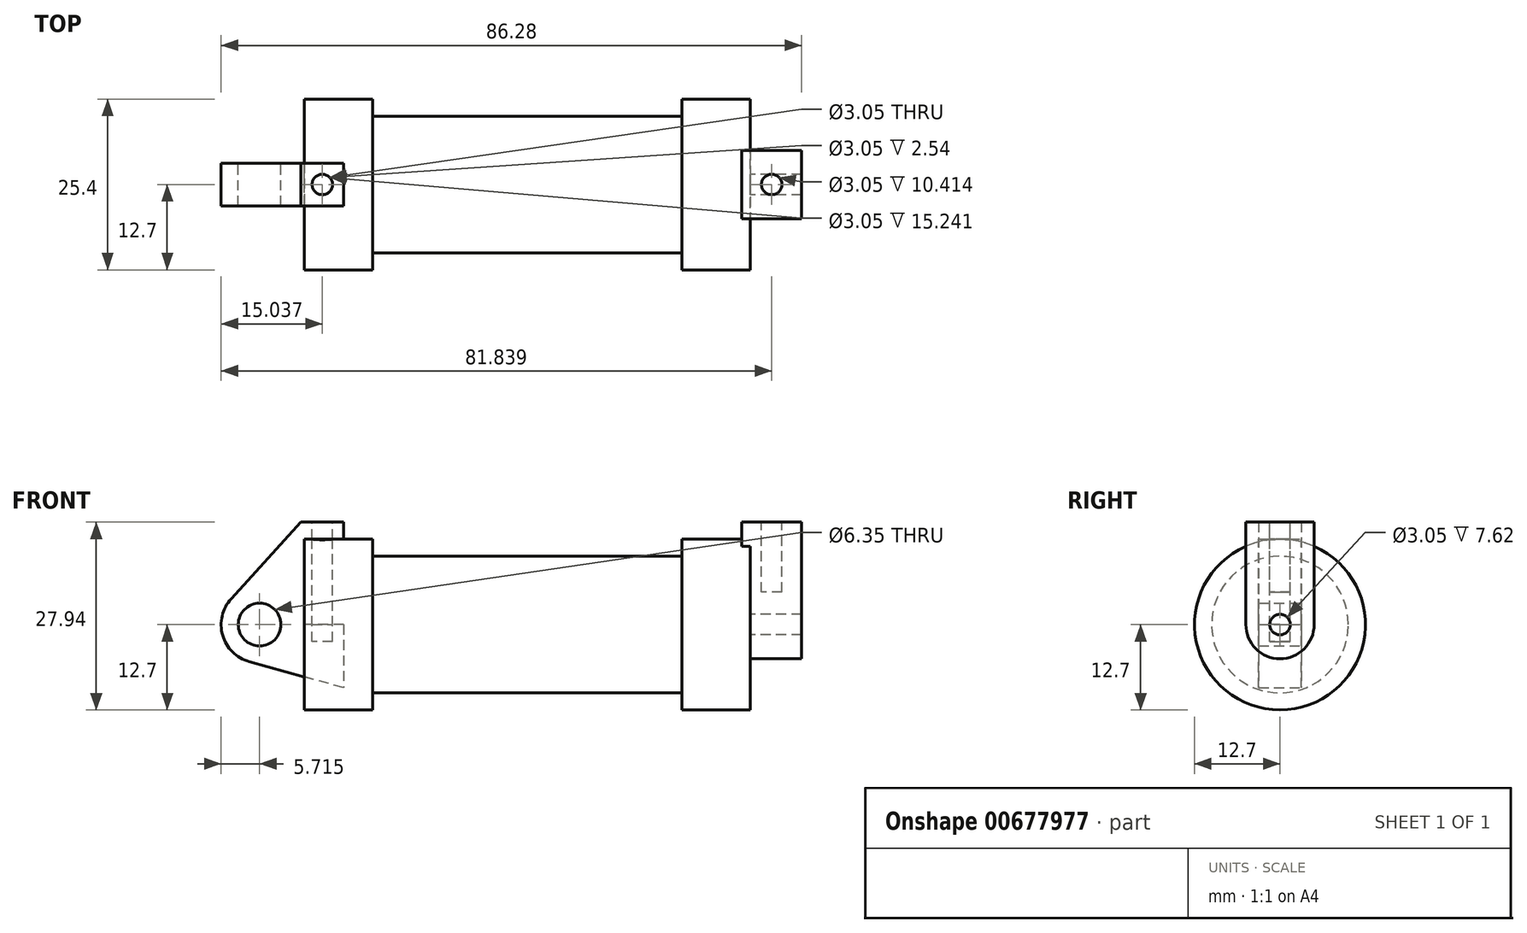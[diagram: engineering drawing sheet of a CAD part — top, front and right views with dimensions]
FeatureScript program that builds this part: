
annotation { "Feature Type Name" : "Feature", "Feature Type Description" : "" }
export const myFeature = defineFeature(function(context is Context, id is Id, definition is map)
    precondition{}
    {
        {
            var Q0;
            Q0=qCreatedBy(makeId("Front.planeOp"),FACE);
            var sketch = newSketch(context, id + "F0", { "sketchPlane" : qUnion([Q0])});
            skLineSegment(sketch, "E0", {"start": v(0, 0) * mm, "end": v(0, 12.7) * mm});
            skLineSegment(sketch, "E1", {"start": v(0, 12.7) * mm, "end": v(10.16, 12.7) * mm});
            skLineSegment(sketch, "E2", {"start": v(10.16, 12.7) * mm, "end": v(10.16, 10.16) * mm});
            skLineSegment(sketch, "E3", {"start": v(10.16, 10.16) * mm, "end": v(56.13, 10.16) * mm});
            skLineSegment(sketch, "E4", {"start": v(56.13, 10.16) * mm, "end": v(56.13, 12.7) * mm});
            skLineSegment(sketch, "E5", {"start": v(56.13, 12.7) * mm, "end": v(66.3, 12.7) * mm});
            skLineSegment(sketch, "E6", {"start": v(66.3, 12.7) * mm, "end": v(66.3, 0) * mm});
            skLineSegment(sketch, "E7", {"start": v(66.3, 0) * mm, "end": v(0, 0) * mm});
            skLineSegment(sketch, "E8", {"start": v(5.84, 15.24) * mm, "end": v(-0.5, 15.24) * mm});
            skLineSegment(sketch, "E9", {"start": v(-0.5, 15.24) * mm, "end": v(-10.88, 3.85) * mm});
            skLineSegment(sketch, "E10", {"start": v(0, 0) * mm, "end": v(-6.65, 0) * mm});
            skCircle(sketch, "E11", {"center": v(-6.65, 0) * mm, "radius": 5.72 * mm});
            skCircle(sketch, "E12", {"center": v(-6.65, 0) * mm, "radius": 3.18 * mm});
            skLineSegment(sketch, "E13", {"start": v(5.84, 15.24) * mm, "end": v(5.84, -9.4) * mm});
            skLineSegment(sketch, "E14", {"start": v(5.84, -9.4) * mm, "end": v(-8.18, -5.5) * mm});
            skSolve(sketch);
        }
        {
            var Q0;
            {var subQ0=sQuery(id+"F0.wireOp",EDGE,"E2");Q0=makeQuery(id+"F0.imprint","IMPRINT",FACE,{"disambiguationData":[TD([[makeQuery(id+"F0.imprint","IMPRINT",EDGE,{"derivedFrom":subQ0}),-1.0]])]});}
            var Q1;
            {var subQ0=sQuery(id+"F0.wireOp",EDGE,"E0");Q1=makeQuery(id+"F0.imprint","IMPRINT",FACE,{"disambiguationData":[TD([[makeQuery(id+"F0.imprint","IMPRINT",EDGE,{"derivedFrom":subQ0}),-1.0]])]});}
            var Q2;
            Q2=sQuery(id+"F0.wireOp",EDGE,"E7");
            revolve(context, id + "F1", {"entities" : qUnion([Q0, Q1]), "axis" : qUnion([Q2]), "revolveType" : RevolveType.FULL});
        }
        {
            var Q0;
            {var subQ0=sQuery(id+"F0.wireOp",EDGE,"E14");Q0=makeQuery(id+"F0.imprint","IMPRINT",FACE,{"disambiguationData":[TD([[makeQuery(id+"F0.imprint","IMPRINT",EDGE,{"derivedFrom":subQ0}),-1.0]])]});}
            var Q1;
            {var subQ1=sQuery(id+"F0.wireOp",EDGE,"E0");Q1=makeQuery(id+"F0.imprint","IMPRINT",FACE,{"disambiguationData":[TD([[makeQuery(id+"F0.imprint","IMPRINT",EDGE,{"derivedFrom":subQ1}),1.0]])]});}
            var Q2;
            {var subQ5=sQuery(id+"F0.wireOp",EDGE,"E12");Q2=makeQuery(id+"F0.imprint","IMPRINT",FACE,{"disambiguationData":[TD([[makeQuery(id+"F0.imprint","IMPRINT",EDGE,{"derivedFrom":subQ5}),-1.0]])]});}
            extrude(context, id + "F2", {"entities" : qUnion([Q0, Q1, Q2]), "endBound" : BoundingType.SYMMETRIC, "depth" : 6.35 * mm, "offsetDistance" : 25.4 * mm});
        }
        {
            var Q0;
            Q0=makeQuery(id+"F1.opRevolve","SWEPT_FACE",FACE,{"disambiguationData":[OSD([sQuery(id+"F0.wireOp",EDGE,"E6")])]});
            var sketch = newSketch(context, id + "F3", { "sketchPlane" : qUnion([Q0])});
            skCircle(sketch, "E15", {"center": v(0, 0) * mm, "radius": 1.52 * mm});
            skCircle(sketch, "E16", {"center": v(0, 0) * mm, "radius": 5.08 * mm});
            skLineSegment(sketch, "E17", {"start": v(-5.08, 0) * mm, "end": v(-5.08, 15.24) * mm});
            skLineSegment(sketch, "E18", {"start": v(5.08, 0) * mm, "end": v(5.08, 15.24) * mm});
            skLineSegment(sketch, "E19", {"start": v(5.08, 15.24) * mm, "end": v(-5.08, 15.24) * mm});
            skSolve(sketch);
        }
        {
            var Q0;
            Q0=makeQuery(id+"F3.imprint","IMPRINT",FACE,{"disambiguationData":[TD([[makeQuery(id+"F3.imprint","IMPRINT",EDGE,{"derivedFrom":sQuery(id+"F3.wireOp",EDGE,"E15")}),-1.0]])]});
            var Q1;
            {var subQ0=sQuery(id+"F3.wireOp",EDGE,"E19");Q1=makeQuery(id+"F3.imprint","IMPRINT",FACE,{"disambiguationData":[TD([[makeQuery(id+"F3.imprint","IMPRINT",EDGE,{"derivedFrom":subQ0}),1.0]])]});}
            var Q2;
            {var subQ0=sQuery(id+"F3.wireOp",EDGE,"E17");var subQ1=sQuery(id+"F3.wireOp",EDGE,"E16");var subQ2=makeQuery(id+"F3.imprint","INTERSECT",VERTEX,{"derivedFrom":[subQ1,subQ0]});Q2=makeQuery(id+"F3.imprint","IMPRINT",FACE,{"disambiguationData":[TD([[makeQuery(id+"F3.imprint","IMPRINT",EDGE,{"disambiguationData":[TD([[subQ2,1.0]])],"derivedFrom":subQ1}),-1.0]])]});}
            extrude(context, id + "F4", {"entities" : qUnion([Q0, Q1, Q2]), "operationType" : NewBodyOperationType.ADD, "depth" : 7.62 * mm, "offsetDistance" : 25.4 * mm, "hasSecondDirection" : true, "secondDirectionOppositeDirection" : true, "secondDirectionDepth" : 1.27 * mm});
        }
        {
            var Q0;
            Q0=makeQuery(id+"F4.opExtrude","SWEPT_FACE",FACE,{"disambiguationData":[OSD([sQuery(id+"F3.wireOp",EDGE,"E19")])]});
            var sketch = newSketch(context, id + "F5", { "sketchPlane" : qUnion([Q0])});
            skCircle(sketch, "E20", {"center": v(69.47, 0) * mm, "radius": 1.52 * mm});
            skPoint(sketch, "E20.centerSnap0", {"position": v(69.47, -5.08) * mm});
            skPoint(sketch, "E20.centerSnap1", {"position": v(65.02, 0) * mm});
            skSolve(sketch);
        }
        {
            var Q0;
            Q0=makeQuery(id+"F5.imprint","IMPRINT",FACE,{"disambiguationData":[TD([[makeQuery(id+"F5.imprint","IMPRINT",EDGE,{"derivedFrom":sQuery(id+"F5.wireOp",EDGE,"E20")}),1.0]])]});
            extrude(context, id + "F6", {"entities" : qUnion([Q0]), "operationType" : NewBodyOperationType.REMOVE, "oppositeDirection" : true, "depth" : 10.4 * mm, "offsetDistance" : 25.4 * mm});
        }
        {
            var Q0;
            Q0=makeQuery(id+"F2.opExtrude","SWEPT_FACE",FACE,{"disambiguationData":[OSD([sQuery(id+"F0.wireOp",EDGE,"E8")])]});
            var sketch = newSketch(context, id + "F7", { "sketchPlane" : qUnion([Q0])});
            skCircle(sketch, "E21", {"center": v(2.67, 0) * mm, "radius": 1.52 * mm});
            skPoint(sketch, "E21.centerSnap0", {"position": v(2.67, -3.18) * mm});
            skPoint(sketch, "E21.centerSnap1", {"position": v(5.84, 0) * mm});
            skSolve(sketch);
        }
        {
            var Q0;
            Q0 = qSketchRegion(id + "F7", true);
            extrude(context, id + "F8", {"entities" : qUnion([Q0]), "operationType" : NewBodyOperationType.REMOVE, "oppositeDirection" : true, "depth" : 17.78 * mm, "offsetDistance" : 25.4 * mm});
        }
    });
